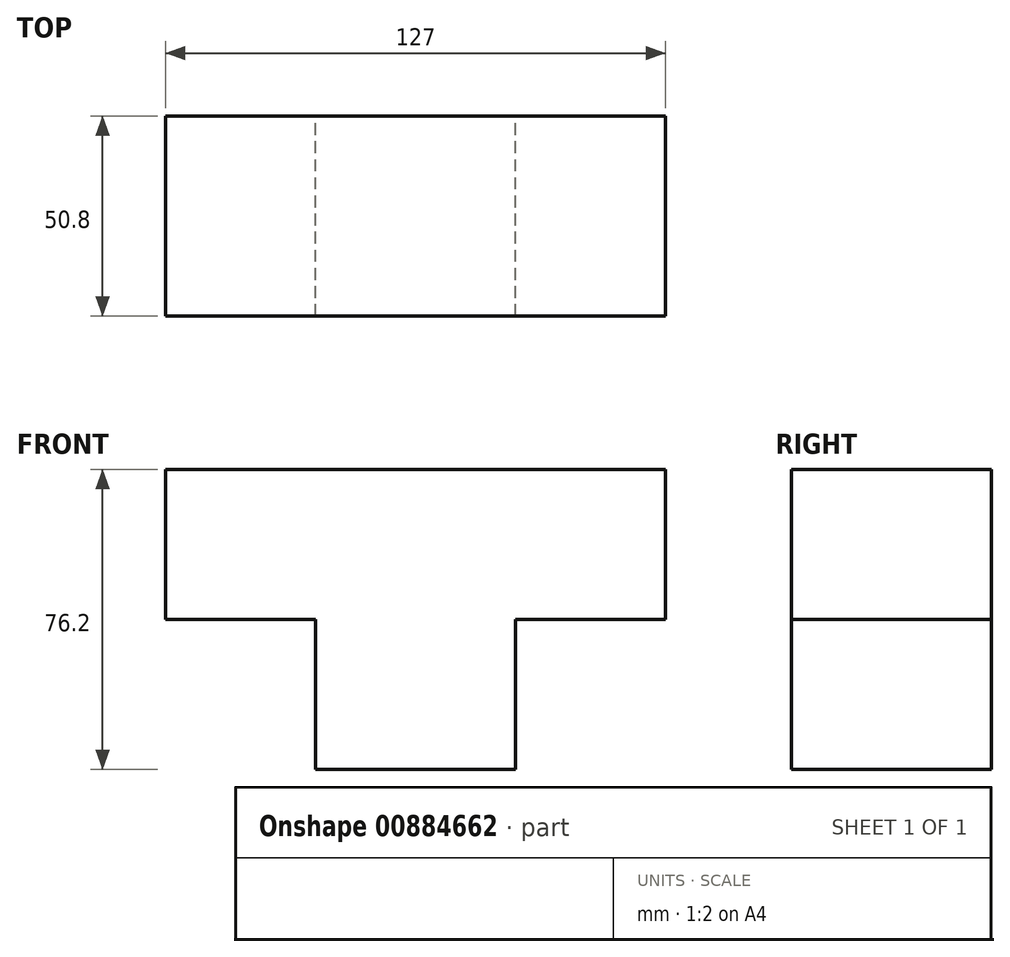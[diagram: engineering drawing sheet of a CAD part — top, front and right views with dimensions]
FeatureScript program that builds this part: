
annotation { "Feature Type Name" : "Feature", "Feature Type Description" : "" }
export const myFeature = defineFeature(function(context is Context, id is Id, definition is map)
    precondition{}
    {
        {
            var Q0;
            Q0=qCreatedBy(makeId("Front.planeOp"),FACE);
            var sketch = newSketch(context, id + "F0", { "sketchPlane" : qUnion([Q0])});
            skLineSegment(sketch, "E0", {"start": v(-21.3, -14.19) * mm, "end": v(29.5, -14.19) * mm});
            skLineSegment(sketch, "E1", {"start": v(29.5, -14.19) * mm, "end": v(29.5, 23.91) * mm});
            skLineSegment(sketch, "E2", {"start": v(29.5, 23.91) * mm, "end": v(67.6, 23.91) * mm});
            skLineSegment(sketch, "E3", {"start": v(67.6, 23.91) * mm, "end": v(67.6, 62.01) * mm});
            skLineSegment(sketch, "E4", {"start": v(-21.3, -14.19) * mm, "end": v(-21.3, 23.91) * mm});
            skLineSegment(sketch, "E5", {"start": v(-21.3, 23.91) * mm, "end": v(-59.4, 23.91) * mm});
            skLineSegment(sketch, "E6", {"start": v(-59.4, 23.91) * mm, "end": v(-59.4, 62.01) * mm});
            skLineSegment(sketch, "E7", {"start": v(-59.4, 62.01) * mm, "end": v(67.6, 62.01) * mm});
            skSolve(sketch);
        }
        {
            var Q0;
            Q0=makeQuery(id+"F0.imprint","IMPRINT",FACE,{"disambiguationData":[TD([[makeQuery(id+"F0.imprint","IMPRINT",EDGE,{"derivedFrom":sQuery(id+"F0.wireOp",EDGE,"E0")}),1.0]])]});
            extrude(context, id + "F1", {"entities" : qUnion([Q0]), "depth" : 50.8 * mm, "offsetDistance" : 25.4 * mm});
        }
    });
